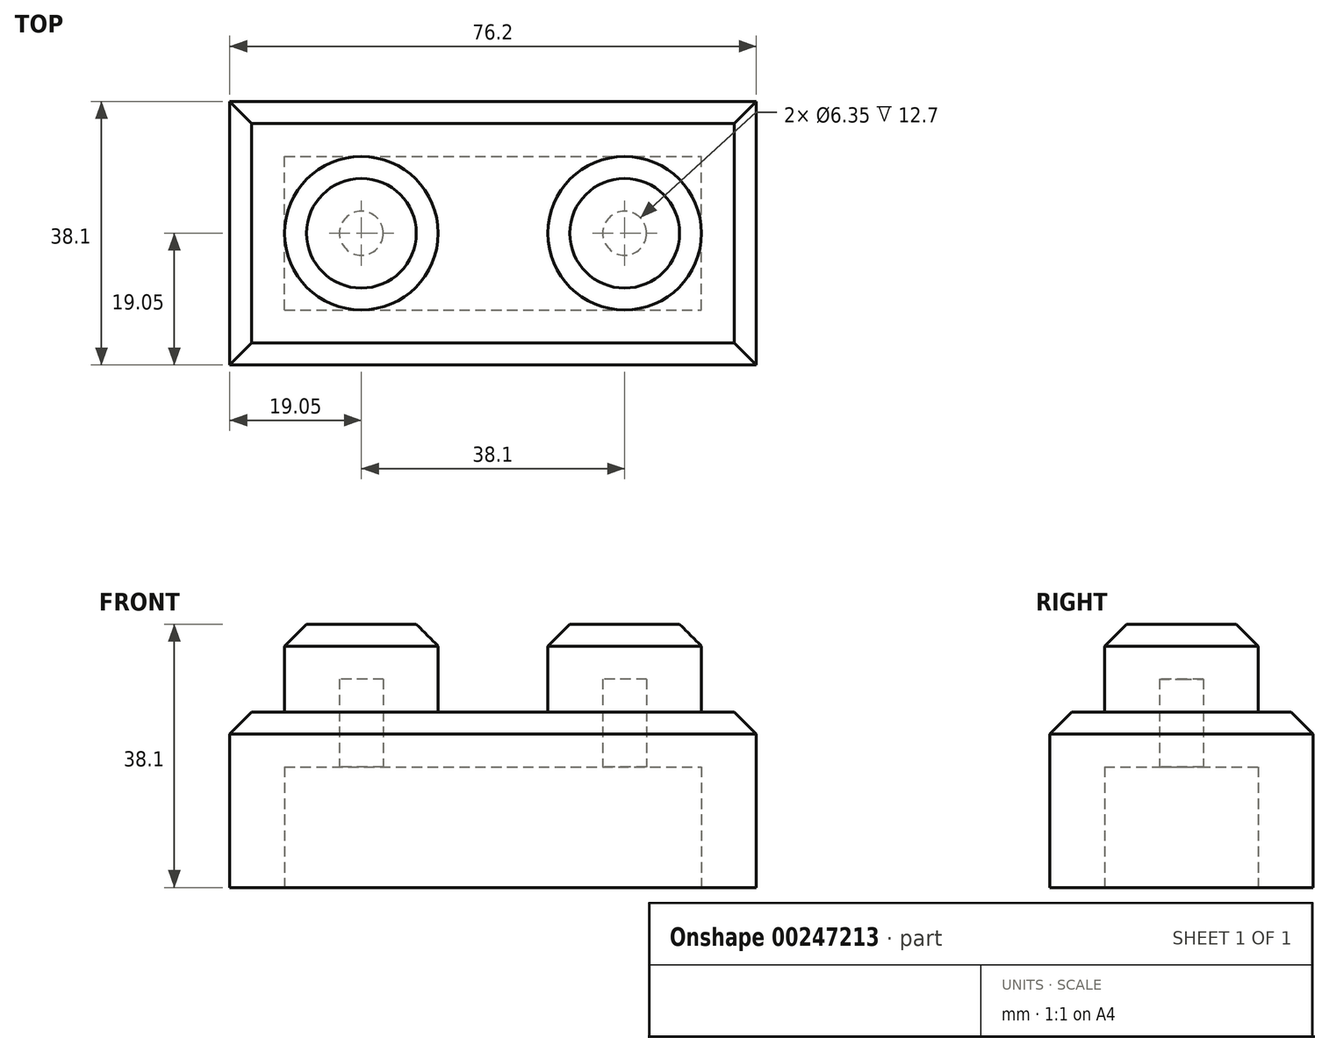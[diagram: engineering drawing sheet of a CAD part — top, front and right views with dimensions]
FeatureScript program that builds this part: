
annotation { "Feature Type Name" : "Feature", "Feature Type Description" : "" }
export const myFeature = defineFeature(function(context is Context, id is Id, definition is map)
    precondition{}
    {
        {
            var Q0;
            Q0=qCreatedBy(makeId("Top.planeOp"),FACE);
            var sketch = newSketch(context, id + "F0", { "sketchPlane" : qUnion([Q0])});
            skLineSegment(sketch, "E0.bottom", {"start": v(0, 0) * mm, "end": v(76.2, 0) * mm});
            skLineSegment(sketch, "E0.top", {"start": v(0, 38.1) * mm, "end": v(76.2, 38.1) * mm});
            skLineSegment(sketch, "E0.left", {"start": v(0, 0) * mm, "end": v(0, 38.1) * mm});
            skLineSegment(sketch, "E0.right", {"start": v(76.2, 0) * mm, "end": v(76.2, 38.1) * mm});
            skSolve(sketch);
        }
        {
            var Q0;
            Q0 = qSketchRegion(id + "F0", true);
            extrude(context, id + "F1", {"entities" : qUnion([Q0]), "depth" : 25.4 * mm});
        }
        {
            var Q0;
            Q0=makeQuery(id+"F1.opExtrude","CAP_FACE",FACE,{"disambiguationData":[OSD([sQuery(id+"F0.wireOp",EDGE,"E0.bottom"),sQuery(id+"F0.wireOp",EDGE,"E0.top"),sQuery(id+"F0.wireOp",EDGE,"E0.left"),sQuery(id+"F0.wireOp",EDGE,"E0.right")])],"isStart":false});
            var sketch = newSketch(context, id + "F2", { "sketchPlane" : qUnion([Q0])});
            skCircle(sketch, "E1", {"center": v(19.05, 19.05) * mm, "radius": 11.11 * mm});
            skPoint(sketch, "E1.centerSnap0", {"position": v(0, 19.05) * mm});
            skCircle(sketch, "E2", {"center": v(57.15, 19.05) * mm, "radius": 11.11 * mm});
            skPoint(sketch, "E2.centerSnap0", {"position": v(76.2, 19.05) * mm});
            skSolve(sketch);
        }
        {
            var Q0;
            Q0=makeQuery(id+"F2.imprint","IMPRINT",FACE,{"disambiguationData":[TD([[makeQuery(id+"F2.imprint","IMPRINT",EDGE,{"derivedFrom":sQuery(id+"F2.wireOp",EDGE,"E2")}),1.0]])]});
            var Q1;
            Q1=makeQuery(id+"F2.imprint","IMPRINT",FACE,{"disambiguationData":[TD([[makeQuery(id+"F2.imprint","IMPRINT",EDGE,{"derivedFrom":sQuery(id+"F2.wireOp",EDGE,"E1")}),1.0]])]});
            extrude(context, id + "F3", {"entities" : qUnion([Q0, Q1]), "operationType" : NewBodyOperationType.ADD, "depth" : 12.7 * mm});
        }
        {
            var Q0;
            Q0=makeQuery(id+"F1.opExtrude","CAP_FACE",FACE,{"disambiguationData":[OSD([sQuery(id+"F0.wireOp",EDGE,"E0.bottom"),sQuery(id+"F0.wireOp",EDGE,"E0.top"),sQuery(id+"F0.wireOp",EDGE,"E0.left"),sQuery(id+"F0.wireOp",EDGE,"E0.right")])],"isStart":true});
            shell(context, id + "F4", {"entities" : qUnion([Q0]), "thickness" : 7.94 * mm});
        }
        {
            var Q0;
            Q0=makeQuery(id+"F1.opExtrude","CAP_EDGE",EDGE,{"disambiguationData":[OSD([sQuery(id+"F0.wireOp",EDGE,"E0.left")])],"isStart":false});
            var Q1;
            Q1=makeQuery(id+"F1.opExtrude","CAP_EDGE",EDGE,{"disambiguationData":[OSD([sQuery(id+"F0.wireOp",EDGE,"E0.right")])],"isStart":false});
            var Q2;
            Q2=makeQuery(id+"F1.opExtrude","CAP_EDGE",EDGE,{"disambiguationData":[OSD([sQuery(id+"F0.wireOp",EDGE,"E0.bottom")])],"isStart":false});
            var Q3;
            Q3=makeQuery(id+"F1.opExtrude","CAP_EDGE",EDGE,{"disambiguationData":[OSD([sQuery(id+"F0.wireOp",EDGE,"E0.top")])],"isStart":false});
            var Q4;
            Q4=makeQuery(id+"F3.opExtrude","CAP_FACE",FACE,{"disambiguationData":[OSD([sQuery(id+"F2.wireOp",EDGE,"E1")])],"isStart":false});
            var Q5;
            Q5=makeQuery(id+"F3.opExtrude","CAP_FACE",FACE,{"disambiguationData":[OSD([sQuery(id+"F2.wireOp",EDGE,"E2")])],"isStart":false});
            chamfer(context, id + "F5", {"entities" : qUnion([Q0, Q1, Q2, Q3, Q4, Q5]), "width" : 3.17 * mm, "tangentPropagation" : true});
        }
    });
